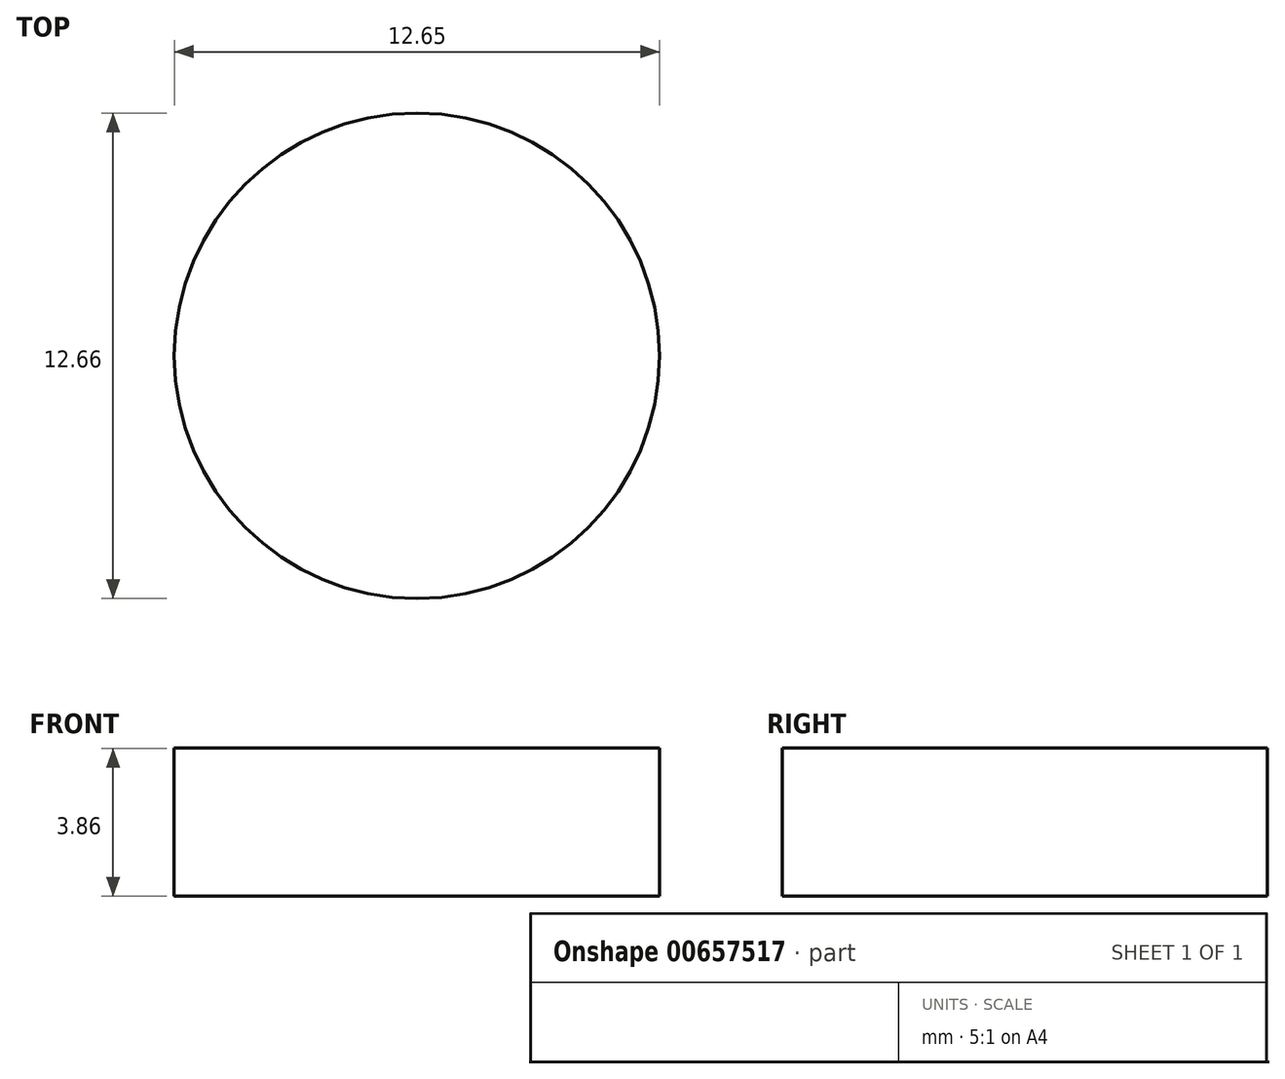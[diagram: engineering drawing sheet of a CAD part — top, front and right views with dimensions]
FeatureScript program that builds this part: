
annotation { "Feature Type Name" : "Feature", "Feature Type Description" : "" }
export const myFeature = defineFeature(function(context is Context, id is Id, definition is map)
    precondition{}
    {
        {
            var Q0;
            Q0=qCreatedBy(makeId("Top.planeOp"),FACE);
            var sketch = newSketch(context, id + "F0", { "sketchPlane" : qUnion([Q0])});
            skCircle(sketch, "E0", {"center": v(-43.38, 36.4) * mm, "radius": 6.33 * mm});
            skSolve(sketch);
        }
        {
            var Q0;
            Q0=makeQuery(id+"F0.imprint","IMPRINT",FACE,{"disambiguationData":[TD([[makeQuery(id+"F0.imprint","IMPRINT",EDGE,{"derivedFrom":sQuery(id+"F0.wireOp",EDGE,"E0")}),1.0]])]});
            extrude(context, id + "F1", {"entities" : qUnion([Q0]), "depth" : 3.86 * mm, "offsetDistance" : 25.4 * mm});
        }
    });
